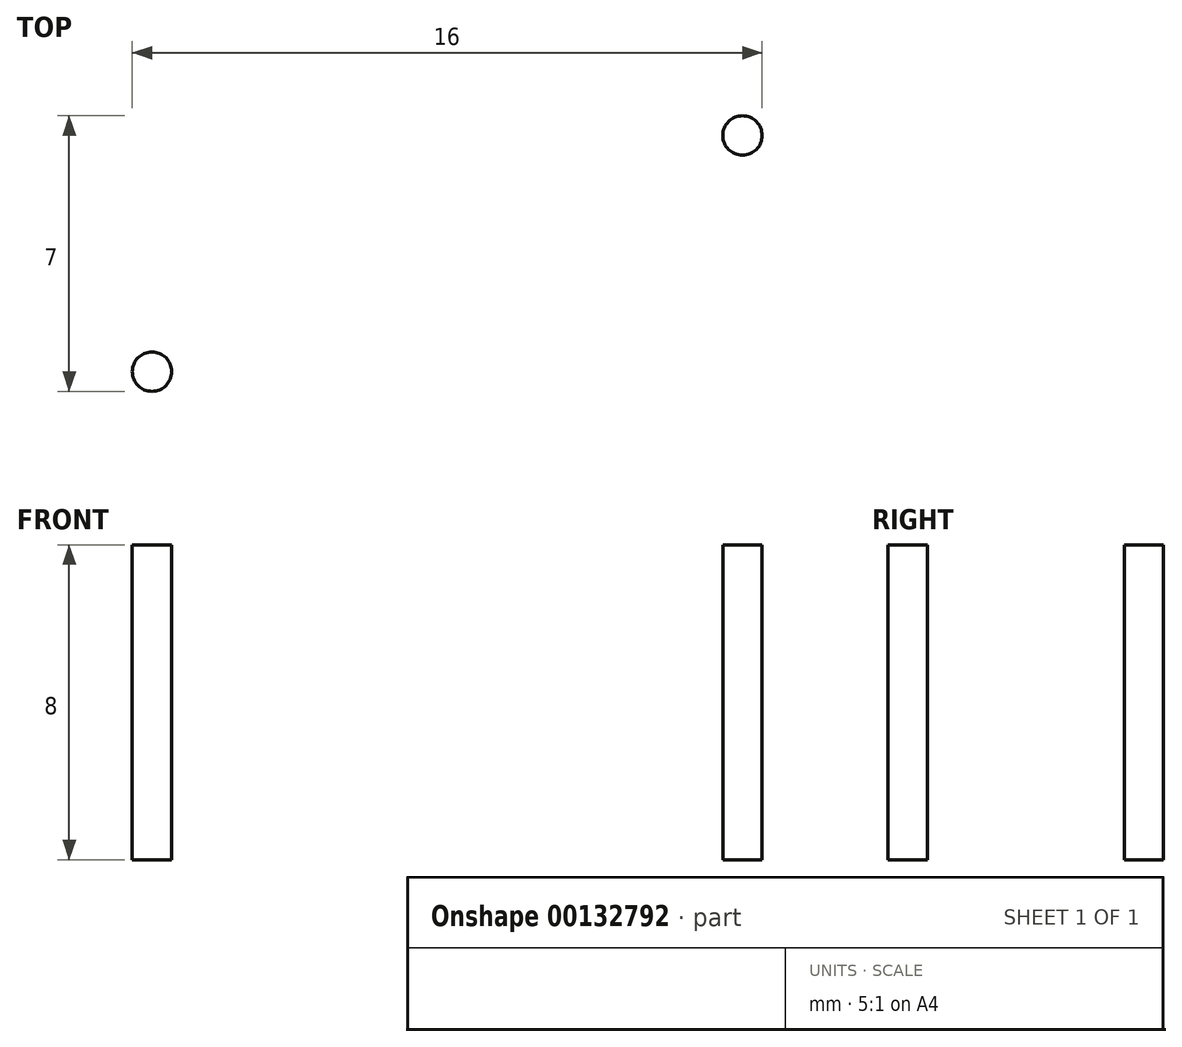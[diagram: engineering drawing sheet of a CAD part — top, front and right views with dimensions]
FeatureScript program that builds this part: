
annotation { "Feature Type Name" : "Feature", "Feature Type Description" : "" }
export const myFeature = defineFeature(function(context is Context, id is Id, definition is map)
    precondition{}
    {
        {
            var Q0;
            Q0=qCreatedBy(makeId("Top.planeOp"),FACE);
            var sketch = newSketch(context, id + "F0", { "sketchPlane" : qUnion([Q0])});
            skCircle(sketch, "E0", {"center": v(-7.5, -3) * mm, "radius": 0.5 * mm});
            skCircle(sketch, "E1.MirrorC", {"center": v(7.5, -3) * mm, "radius": 0.5 * mm});
            skCircle(sketch, "E2.MirrorC", {"center": v(-7.5, 3) * mm, "radius": 0.5 * mm});
            skCircle(sketch, "E3.MirrorC", {"center": v(7.5, 3) * mm, "radius": 0.5 * mm});
            skSolve(sketch);
        }
        {
            var Q0;
            Q0=makeQuery(id+"F0.imprint","IMPRINT",FACE,{"disambiguationData":[TD([[makeQuery(id+"F0.imprint","IMPRINT",EDGE,{"derivedFrom":sQuery(id+"F0.wireOp",EDGE,"E0")}),1.0]])]});
            var Q1;
            Q1=makeQuery(id+"F0.imprint","IMPRINT",FACE,{"disambiguationData":[TD([[makeQuery(id+"F0.imprint","IMPRINT",EDGE,{"derivedFrom":sQuery(id+"F0.wireOp",EDGE,"E1.MirrorC")}),-1.0]])]});
            var Q2;
            Q2=makeQuery(id+"F0.imprint","IMPRINT",FACE,{"disambiguationData":[TD([[makeQuery(id+"F0.imprint","IMPRINT",EDGE,{"derivedFrom":sQuery(id+"F0.wireOp",EDGE,"E3.MirrorC")}),1.0]])]});
            var Q3;
            Q3=makeQuery(id+"F0.imprint","IMPRINT",FACE,{"disambiguationData":[TD([[makeQuery(id+"F0.imprint","IMPRINT",EDGE,{"derivedFrom":sQuery(id+"F0.wireOp",EDGE,"E2.MirrorC")}),-1.0]])]});
            extrude(context, id + "F1", {"entities" : qUnion([Q0, Q1, Q2, Q3]), "depth" : 3 * mm, "hasSecondDirection" : true, "secondDirectionOppositeDirection" : true, "secondDirectionDepth" : 5 * mm});
        }
    });
